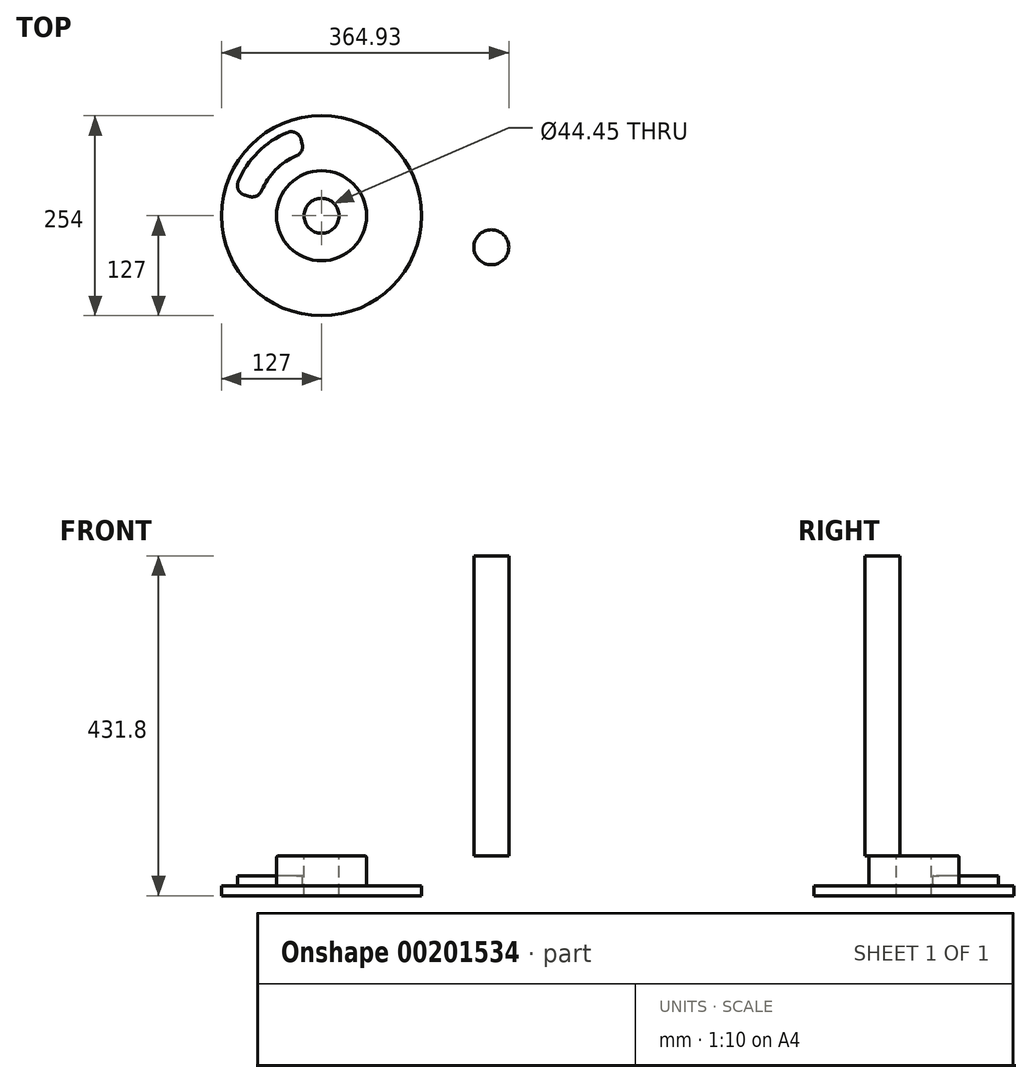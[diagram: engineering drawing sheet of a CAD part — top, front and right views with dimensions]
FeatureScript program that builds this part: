
annotation { "Feature Type Name" : "Feature", "Feature Type Description" : "" }
export const myFeature = defineFeature(function(context is Context, id is Id, definition is map)
    precondition{}
    {
        {
            var Q0;
            Q0=qCreatedBy(makeId("Top.planeOp"),FACE);
            var sketch = newSketch(context, id + "F0", { "sketchPlane" : qUnion([Q0])});
            skCircle(sketch, "E0", {"center": v(0, 0) * mm, "radius": 127 * mm});
            skSolve(sketch);
        }
        {
            var Q0;
            Q0=makeQuery(id+"F0.imprint","IMPRINT",FACE,{"disambiguationData":[TD([[makeQuery(id+"F0.imprint","IMPRINT",EDGE,{"derivedFrom":sQuery(id+"F0.wireOp",EDGE,"E0")}),1.0]])]});
            extrude(context, id + "F1", {"entities" : qUnion([Q0]), "depth" : 25.4 * mm});
        }
        {
            var Q0;
            Q0=makeQuery(id+"F1.opExtrude","CAP_FACE",FACE,{"disambiguationData":[OSD([sQuery(id+"F0.wireOp",EDGE,"E0")])],"isStart":false});
            var sketch = newSketch(context, id + "F2", { "sketchPlane" : qUnion([Q0])});
            skCircle(sketch, "E1", {"center": v(0, 0) * mm, "radius": 57.15 * mm});
            skSolve(sketch);
        }
        {
            var Q0;
            Q0=makeQuery(id+"F2.imprint","IMPRINT",FACE,{"disambiguationData":[TD([[makeQuery(id+"F2.imprint","IMPRINT",EDGE,{"derivedFrom":sQuery(id+"F2.wireOp",EDGE,"E1")}),1.0]])]});
            extrude(context, id + "F3", {"entities" : qUnion([Q0]), "operationType" : NewBodyOperationType.ADD, "depth" : 25.4 * mm});
        }
        {
            var Q0;
            Q0=makeQuery(id+"F1.opExtrude","CAP_FACE",FACE,{"disambiguationData":[OSD([sQuery(id+"F0.wireOp",EDGE,"E0")])],"isStart":false});
            var sketch = newSketch(context, id + "F4", { "sketchPlane" : qUnion([Q0])});
            skLineSegment(sketch, "E2", {"start": v(0, 127) * mm, "end": v(0, -127) * mm, "construction": true});
            skLineSegment(sketch, "E3", {"start": v(-127, 0) * mm, "end": v(127, 0) * mm, "construction": true});
            skArc(sketch, "E4", {"start": v(-105.84, 43.15) * mm, "mid": v(-80.82, 80.82) * mm, "end": v(-43.15, 105.84) * mm});
            skArc(sketch, "E5", {"start": v(-76.18, 31.8) * mm, "mid": v(-58.37, 58.37) * mm, "end": v(-31.8, 76.18) * mm});
            skLineSegment(sketch, "E6", {"start": v(-91.18, 24.43) * mm, "end": v(-97.37, 26.09) * mm});
            skLineSegment(sketch, "E7", {"start": v(-24.43, 91.18) * mm, "end": v(-26.09, 97.37) * mm});
            skPoint(sketch, "E8.visualSharp", {"position": v(-29.58, 110.4) * mm});
            skArc(sketch, "E8.filletArc", {"start": v(-26.09, 97.37) * mm, "mid": v(-32.7, 105.46) * mm, "end": v(-43.15, 105.84) * mm});
            skPoint(sketch, "E9.visualSharp", {"position": v(-21.37, 79.74) * mm});
            skArc(sketch, "E9.filletArc", {"start": v(-31.8, 76.18) * mm, "mid": v(-25.3, 82.3) * mm, "end": v(-24.43, 91.18) * mm});
            skPoint(sketch, "E10.visualSharp", {"position": v(-110.4, 29.58) * mm});
            skArc(sketch, "E10.filletArc", {"start": v(-105.84, 43.15) * mm, "mid": v(-105.46, 32.7) * mm, "end": v(-97.37, 26.09) * mm});
            skPoint(sketch, "E11.visualSharp", {"position": v(-79.74, 21.37) * mm});
            skArc(sketch, "E11.filletArc", {"start": v(-91.18, 24.43) * mm, "mid": v(-82.3, 25.3) * mm, "end": v(-76.18, 31.8) * mm});
            skLineSegment(sketch, "E12.MirrorCS", {"start": v(91.18, 24.43) * mm, "end": v(97.37, 26.09) * mm});
            skLineSegment(sketch, "E13.MirrorCS", {"start": v(24.43, 91.18) * mm, "end": v(26.09, 97.37) * mm});
            skArc(sketch, "E14.MirrorCS", {"start": v(26.09, 97.37) * mm, "mid": v(32.7, 105.46) * mm, "end": v(43.15, 105.84) * mm});
            skArc(sketch, "E15.MirrorCS", {"start": v(31.8, 76.18) * mm, "mid": v(25.3, 82.3) * mm, "end": v(24.43, 91.18) * mm});
            skArc(sketch, "E16.MirrorCS", {"start": v(105.84, 43.15) * mm, "mid": v(105.46, 32.7) * mm, "end": v(97.37, 26.09) * mm});
            skArc(sketch, "E17.MirrorCS", {"start": v(76.18, 31.8) * mm, "mid": v(58.37, 58.37) * mm, "end": v(31.8, 76.18) * mm});
            skArc(sketch, "E18.MirrorCS", {"start": v(105.84, 43.15) * mm, "mid": v(80.82, 80.82) * mm, "end": v(43.15, 105.84) * mm});
            skArc(sketch, "E19.MirrorCS", {"start": v(91.18, 24.43) * mm, "mid": v(82.3, 25.3) * mm, "end": v(76.18, 31.8) * mm});
            skPoint(sketch, "E20.MirrorP", {"position": v(110.4, 29.58) * mm});
            skPoint(sketch, "E21.MirrorP", {"position": v(79.74, 21.37) * mm});
            skPoint(sketch, "E22.MirrorP", {"position": v(29.58, 110.4) * mm});
            skPoint(sketch, "E23.MirrorP", {"position": v(21.37, 79.74) * mm});
            skLineSegment(sketch, "E24.MirrorCS", {"start": v(24.43, -91.18) * mm, "end": v(26.09, -97.37) * mm});
            skLineSegment(sketch, "E25.MirrorCS", {"start": v(91.18, -24.43) * mm, "end": v(97.37, -26.09) * mm});
            skLineSegment(sketch, "E26.MirrorCS", {"start": v(-24.43, -91.18) * mm, "end": v(-26.09, -97.37) * mm});
            skLineSegment(sketch, "E27.MirrorCS", {"start": v(-91.18, -24.43) * mm, "end": v(-97.37, -26.09) * mm});
            skPoint(sketch, "E28.MirrorP", {"position": v(110.4, -29.58) * mm});
            skPoint(sketch, "E29.MirrorP", {"position": v(-29.58, -110.4) * mm});
            skPoint(sketch, "E30.MirrorP", {"position": v(29.58, -110.4) * mm});
            skPoint(sketch, "E31.MirrorP", {"position": v(-21.37, -79.74) * mm});
            skArc(sketch, "E32.MirrorCS", {"start": v(91.18, -24.43) * mm, "mid": v(82.3, -25.3) * mm, "end": v(76.18, -31.8) * mm});
            skPoint(sketch, "E33.MirrorP", {"position": v(-110.4, -29.58) * mm});
            skPoint(sketch, "E34.MirrorP", {"position": v(-79.74, -21.37) * mm});
            skArc(sketch, "E35.MirrorCS", {"start": v(26.09, -97.37) * mm, "mid": v(32.7, -105.46) * mm, "end": v(43.15, -105.84) * mm});
            skArc(sketch, "E36.MirrorCS", {"start": v(-91.18, -24.43) * mm, "mid": v(-82.3, -25.3) * mm, "end": v(-76.18, -31.8) * mm});
            skArc(sketch, "E37.MirrorCS", {"start": v(-105.84, -43.15) * mm, "mid": v(-105.46, -32.7) * mm, "end": v(-97.37, -26.09) * mm});
            skArc(sketch, "E38.MirrorCS", {"start": v(105.84, -43.15) * mm, "mid": v(105.46, -32.7) * mm, "end": v(97.37, -26.09) * mm});
            skPoint(sketch, "E39.MirrorP", {"position": v(79.74, -21.37) * mm});
            skArc(sketch, "E40.MirrorCS", {"start": v(31.8, -76.18) * mm, "mid": v(25.3, -82.3) * mm, "end": v(24.43, -91.18) * mm});
            skArc(sketch, "E41.MirrorCS", {"start": v(76.18, -31.8) * mm, "mid": v(58.37, -58.37) * mm, "end": v(31.8, -76.18) * mm});
            skArc(sketch, "E42.MirrorCS", {"start": v(-105.84, -43.15) * mm, "mid": v(-80.82, -80.82) * mm, "end": v(-43.15, -105.84) * mm});
            skArc(sketch, "E43.MirrorCS", {"start": v(-31.8, -76.18) * mm, "mid": v(-25.3, -82.3) * mm, "end": v(-24.43, -91.18) * mm});
            skArc(sketch, "E44.MirrorCS", {"start": v(-76.18, -31.8) * mm, "mid": v(-58.37, -58.37) * mm, "end": v(-31.8, -76.18) * mm});
            skPoint(sketch, "E45.MirrorP", {"position": v(21.37, -79.74) * mm});
            skArc(sketch, "E46.MirrorCS", {"start": v(105.84, -43.15) * mm, "mid": v(80.82, -80.82) * mm, "end": v(43.15, -105.84) * mm});
            skArc(sketch, "E47.MirrorCS", {"start": v(-26.09, -97.37) * mm, "mid": v(-32.7, -105.46) * mm, "end": v(-43.15, -105.84) * mm});
            skSolve(sketch);
        }
        {
            var Q0;
            Q0=makeQuery(id+"F4.imprint","IMPRINT",FACE,{"disambiguationData":[TD([[makeQuery(id+"F4.imprint","IMPRINT",EDGE,{"derivedFrom":sQuery(id+"F4.wireOp",EDGE,"E4")}),-1.0]])]});
            var Q1;
            Q1=makeQuery(id+"F4.imprint","IMPRINT",FACE,{"disambiguationData":[TD([[makeQuery(id+"F4.imprint","IMPRINT",EDGE,{"derivedFrom":sQuery(id+"F4.wireOp",EDGE,"E12.MirrorCS")}),1.0]])]});
            var Q2;
            Q2=makeQuery(id+"F4.imprint","IMPRINT",FACE,{"disambiguationData":[TD([[makeQuery(id+"F4.imprint","IMPRINT",EDGE,{"derivedFrom":sQuery(id+"F4.wireOp",EDGE,"E26.MirrorCS")}),-1.0]])]});
            var Q3;
            Q3=makeQuery(id+"F4.imprint","IMPRINT",FACE,{"disambiguationData":[TD([[makeQuery(id+"F4.imprint","IMPRINT",EDGE,{"derivedFrom":sQuery(id+"F4.wireOp",EDGE,"E24.MirrorCS")}),1.0]])]});
            extrude(context, id + "F5", {"entities" : qUnion([Q0, Q1, Q2, Q3]), "operationType" : NewBodyOperationType.REMOVE, "oppositeDirection" : true, "depth" : 12.7 * mm});
        }
        {
            var Q0;
            Q0=makeQuery(id+"F1.opExtrude","CAP_EDGE",EDGE,{"disambiguationData":[OSD([sQuery(id+"F0.wireOp",EDGE,"E0")])],"isStart":false});
            var Q1;
            Q1=makeQuery(id+"F3.opExtrude","CAP_EDGE",EDGE,{"disambiguationData":[OSD([sQuery(id+"F2.wireOp",EDGE,"E1")])],"isStart":true});
            var Q2;
            Q2=makeQuery(id+"F3.opExtrude","CAP_EDGE",EDGE,{"disambiguationData":[OSD([sQuery(id+"F2.wireOp",EDGE,"E1")])],"isStart":false});
            var Q3;
            Q3=makeQuery(id+"F5.boolean.opBoolean","COPY",EDGE,{"derivedFrom":makeQuery(id+"F5.opExtrude","CAP_EDGE",EDGE,{"disambiguationData":[OSD([sQuery(id+"F4.wireOp",EDGE,"E4")])],"isStart":true})});
            var Q4;
            Q4=makeQuery(id+"F5.boolean.opBoolean","COPY",EDGE,{"derivedFrom":makeQuery(id+"F5.opExtrude","CAP_EDGE",EDGE,{"disambiguationData":[OSD([sQuery(id+"F4.wireOp",EDGE,"E8.filletArc")])],"isStart":true})});
            var Q5;
            Q5=makeQuery(id+"F5.boolean.opBoolean","COPY",EDGE,{"derivedFrom":makeQuery(id+"F5.opExtrude","CAP_EDGE",EDGE,{"disambiguationData":[OSD([sQuery(id+"F4.wireOp",EDGE,"E14.MirrorCS")])],"isStart":true})});
            var Q6;
            Q6=makeQuery(id+"F5.boolean.opBoolean","COPY",EDGE,{"derivedFrom":makeQuery(id+"F5.opExtrude","CAP_EDGE",EDGE,{"disambiguationData":[OSD([sQuery(id+"F4.wireOp",EDGE,"E25.MirrorCS")])],"isStart":true})});
            var Q7;
            Q7=makeQuery(id+"F5.boolean.opBoolean","COPY",EDGE,{"derivedFrom":makeQuery(id+"F5.opExtrude","CAP_EDGE",EDGE,{"disambiguationData":[OSD([sQuery(id+"F4.wireOp",EDGE,"E27.MirrorCS")])],"isStart":true})});
            var Q8;
            Q8=makeQuery(id+"F5.boolean.opBoolean","COPY",EDGE,{"derivedFrom":makeQuery(id+"F5.opExtrude","CAP_EDGE",EDGE,{"disambiguationData":[OSD([sQuery(id+"F4.wireOp",EDGE,"E4")])],"isStart":false})});
            var Q9;
            Q9=makeQuery(id+"F5.boolean.opBoolean","COPY",EDGE,{"derivedFrom":makeQuery(id+"F5.opExtrude","CAP_EDGE",EDGE,{"disambiguationData":[OSD([sQuery(id+"F4.wireOp",EDGE,"E18.MirrorCS")])],"isStart":false})});
            var Q10;
            Q10=makeQuery(id+"F5.boolean.opBoolean","COPY",EDGE,{"derivedFrom":makeQuery(id+"F5.opExtrude","CAP_EDGE",EDGE,{"disambiguationData":[OSD([sQuery(id+"F4.wireOp",EDGE,"E32.MirrorCS")])],"isStart":false})});
            var Q11;
            Q11=makeQuery(id+"F5.boolean.opBoolean","COPY",EDGE,{"derivedFrom":makeQuery(id+"F5.opExtrude","CAP_EDGE",EDGE,{"disambiguationData":[OSD([sQuery(id+"F4.wireOp",EDGE,"E44.MirrorCS")])],"isStart":false})});
            fillet(context, id + "F6", {"entities" : qUnion([Q0, Q1, Q2, Q3, Q4, Q5, Q6, Q7, Q8, Q9, Q10, Q11]), "radius" : 2.54 * mm, "tangentPropagation" : true, "allowEdgeOverflow" : false});
        }
        {
            var Q0;
            Q0=makeQuery(id+"F3.opExtrude","CAP_FACE",FACE,{"disambiguationData":[OSD([sQuery(id+"F2.wireOp",EDGE,"E1")])],"isStart":false});
            var sketch = newSketch(context, id + "F7", { "sketchPlane" : qUnion([Q0])});
            skCircle(sketch, "E48", {"center": v(0, 0) * mm, "radius": 22.23 * mm});
            skSolve(sketch);
        }
        {
            var Q0;
            Q0=makeQuery(id+"F7.imprint","IMPRINT",FACE,{"disambiguationData":[TD([[makeQuery(id+"F7.imprint","IMPRINT",EDGE,{"derivedFrom":sQuery(id+"F7.wireOp",EDGE,"E48")}),1.0]])]});
            extrude(context, id + "F8", {"entities" : qUnion([Q0]), "operationType" : NewBodyOperationType.REMOVE, "endBound" : BoundingType.THROUGH_ALL, "oppositeDirection" : true, "depth" : 25.4 * mm});
        }
        {
            var Q0;
            Q0=makeQuery(id+"F3.opExtrude","CAP_FACE",FACE,{"disambiguationData":[OSD([sQuery(id+"F2.wireOp",EDGE,"E1")])],"isStart":false});
            var sketch = newSketch(context, id + "F9", { "sketchPlane" : qUnion([Q0])});
            skCircle(sketch, "E49", {"center": v(215.7, -40) * mm, "radius": 22.23 * mm});
            skSolve(sketch);
        }
        {
            var Q0;
            Q0=makeQuery(id+"F9.imprint","IMPRINT",FACE,{"disambiguationData":[TD([[makeQuery(id+"F9.imprint","IMPRINT",EDGE,{"derivedFrom":sQuery(id+"F9.wireOp",EDGE,"E49")}),1.0]])]});
            extrude(context, id + "F10", {"entities" : qUnion([Q0]), "depth" : 381 * mm});
        }
    });
